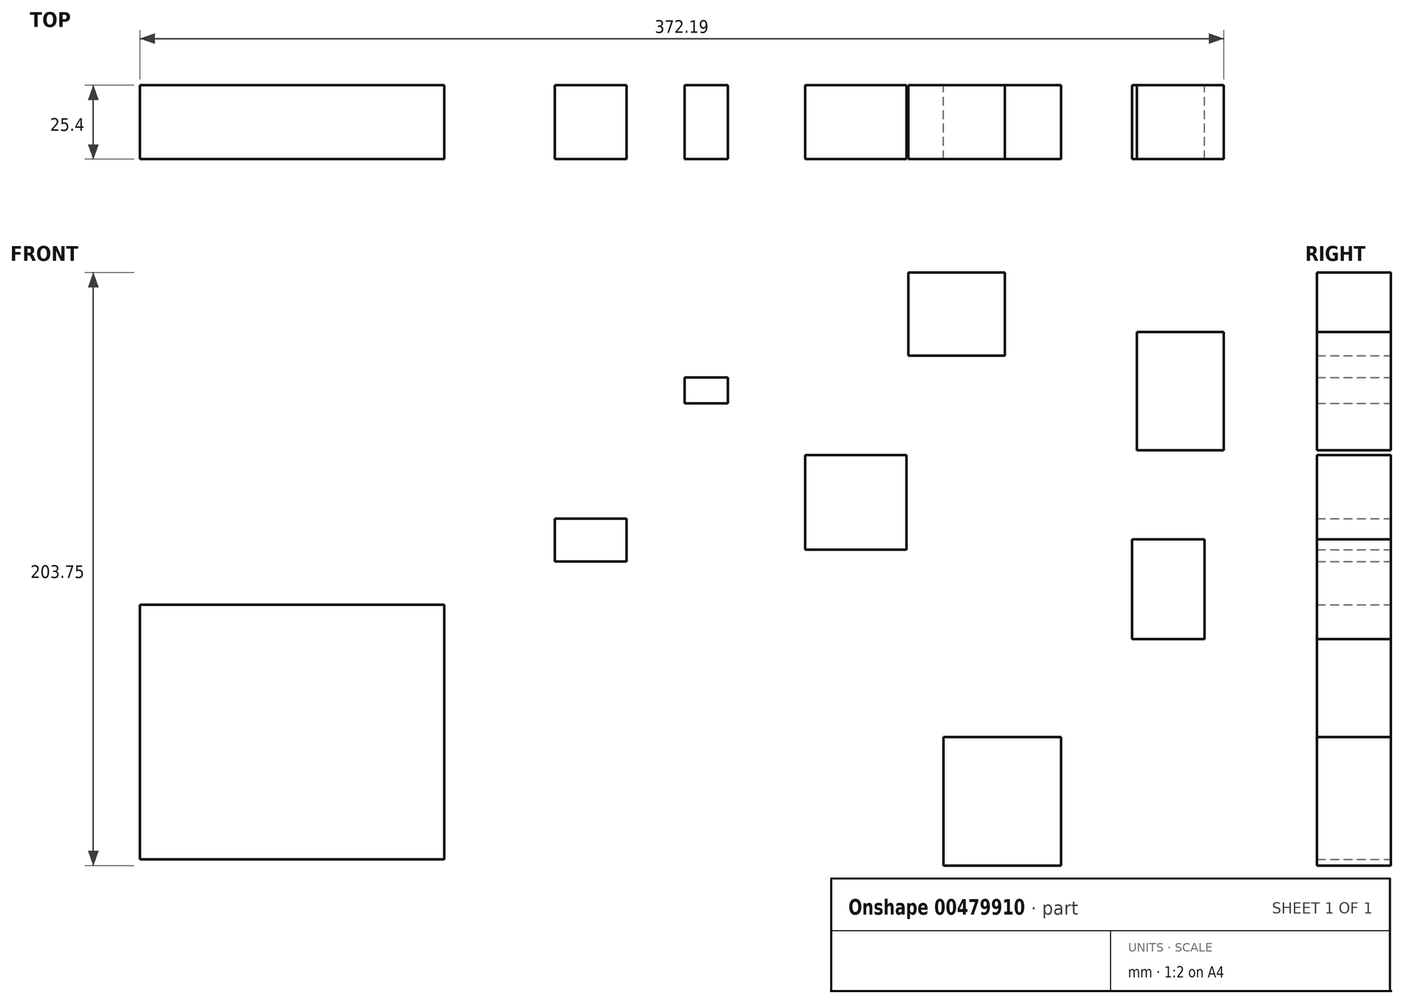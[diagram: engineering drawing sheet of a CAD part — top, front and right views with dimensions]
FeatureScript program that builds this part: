
annotation { "Feature Type Name" : "Feature", "Feature Type Description" : "" }
export const myFeature = defineFeature(function(context is Context, id is Id, definition is map)
    precondition{}
    {
        {
            var Q0;
            Q0=qCreatedBy(makeId("Front.planeOp"),FACE);
            var sketch = newSketch(context, id + "F0", { "sketchPlane" : qUnion([Q0])});
            skLineSegment(sketch, "E0.bottom", {"start": v(-37.89, 11.16) * mm, "end": v(-142.44, 11.16) * mm});
            skLineSegment(sketch, "E0.top", {"start": v(-37.89, 98.68) * mm, "end": v(-142.44, 98.68) * mm});
            skLineSegment(sketch, "E0.left", {"start": v(-37.89, 11.16) * mm, "end": v(-37.89, 98.68) * mm});
            skLineSegment(sketch, "E0.right", {"start": v(-142.44, 11.16) * mm, "end": v(-142.44, 98.68) * mm});
            skPoint(sketch, "E0.middle", {"position": v(-90.16, 54.92) * mm});
            skLineSegment(sketch, "E1.bottom", {"start": v(0, 128.23) * mm, "end": v(24.67, 128.23) * mm});
            skLineSegment(sketch, "E1.top", {"start": v(0, 113.55) * mm, "end": v(24.67, 113.55) * mm});
            skLineSegment(sketch, "E1.left", {"start": v(0, 128.23) * mm, "end": v(0, 113.55) * mm});
            skLineSegment(sketch, "E1.right", {"start": v(24.67, 128.23) * mm, "end": v(24.67, 113.55) * mm});
            skLineSegment(sketch, "E2.bottom", {"start": v(86.03, 150.06) * mm, "end": v(120.85, 150.06) * mm});
            skLineSegment(sketch, "E2.top", {"start": v(86.03, 117.55) * mm, "end": v(120.85, 117.55) * mm});
            skLineSegment(sketch, "E2.left", {"start": v(86.03, 150.06) * mm, "end": v(86.03, 117.55) * mm});
            skLineSegment(sketch, "E2.right", {"start": v(120.85, 150.06) * mm, "end": v(120.85, 117.55) * mm});
            skLineSegment(sketch, "E3.bottom", {"start": v(44.57, 176.78) * mm, "end": v(59.5, 176.78) * mm});
            skLineSegment(sketch, "E3.top", {"start": v(44.57, 167.83) * mm, "end": v(59.5, 167.83) * mm});
            skLineSegment(sketch, "E3.left", {"start": v(44.57, 176.78) * mm, "end": v(44.57, 167.83) * mm});
            skLineSegment(sketch, "E3.right", {"start": v(59.5, 176.78) * mm, "end": v(59.5, 167.83) * mm});
            skLineSegment(sketch, "E4.bottom", {"start": v(121.4, 212.79) * mm, "end": v(154.57, 212.79) * mm});
            skLineSegment(sketch, "E4.top", {"start": v(121.4, 184.22) * mm, "end": v(154.57, 184.22) * mm});
            skLineSegment(sketch, "E4.left", {"start": v(121.4, 212.79) * mm, "end": v(121.4, 184.22) * mm});
            skLineSegment(sketch, "E4.right", {"start": v(154.57, 212.79) * mm, "end": v(154.57, 184.22) * mm});
            skLineSegment(sketch, "E5.bottom", {"start": v(199.9, 192.33) * mm, "end": v(229.75, 192.33) * mm});
            skLineSegment(sketch, "E5.top", {"start": v(199.9, 151.75) * mm, "end": v(229.75, 151.75) * mm});
            skLineSegment(sketch, "E5.left", {"start": v(199.9, 192.33) * mm, "end": v(199.9, 151.75) * mm});
            skLineSegment(sketch, "E5.right", {"start": v(229.75, 192.33) * mm, "end": v(229.75, 151.75) * mm});
            skLineSegment(sketch, "E6.bottom", {"start": v(198.24, 121.1) * mm, "end": v(223.12, 121.1) * mm});
            skLineSegment(sketch, "E6.top", {"start": v(198.24, 86.81) * mm, "end": v(223.12, 86.81) * mm});
            skLineSegment(sketch, "E6.left", {"start": v(198.24, 121.1) * mm, "end": v(198.24, 86.81) * mm});
            skLineSegment(sketch, "E6.right", {"start": v(223.12, 121.1) * mm, "end": v(223.12, 86.81) * mm});
            skLineSegment(sketch, "E7.bottom", {"start": v(133.57, 53.22) * mm, "end": v(173.92, 53.22) * mm});
            skLineSegment(sketch, "E7.top", {"start": v(133.57, 9.04) * mm, "end": v(173.92, 9.04) * mm});
            skLineSegment(sketch, "E7.left", {"start": v(133.57, 53.22) * mm, "end": v(133.57, 9.04) * mm});
            skLineSegment(sketch, "E7.right", {"start": v(173.92, 53.22) * mm, "end": v(173.92, 9.04) * mm});
            skFitSpline(sketch, "E8", {"points": [v(-303.13, 44.26) * mm, v(-250.39, 79.69) * mm, v(-245.66, 68.66) * mm, v(-203.94, 84.4) * mm, v(-194.5, 147.39) * mm, v(-150.4, 113.54) * mm], "startDerivative": vector(299.55, 248.45) * mm, "endDerivative": vector(257.92, -269.81) * mm});
            skSolve(sketch);
        }
        {
            var Q0;
            Q0 = qSketchRegion(id + "F0", true);
            extrude(context, id + "F1", {"entities" : qUnion([Q0]), "depth" : 25.4 * mm});
        }
        {
            var Q0;
            Q0 = qSketchRegion(id + "F0", true);
            extrude(context, id + "F2", {"entities" : qUnion([Q0]), "depth" : 25.4 * mm});
        }
    });
